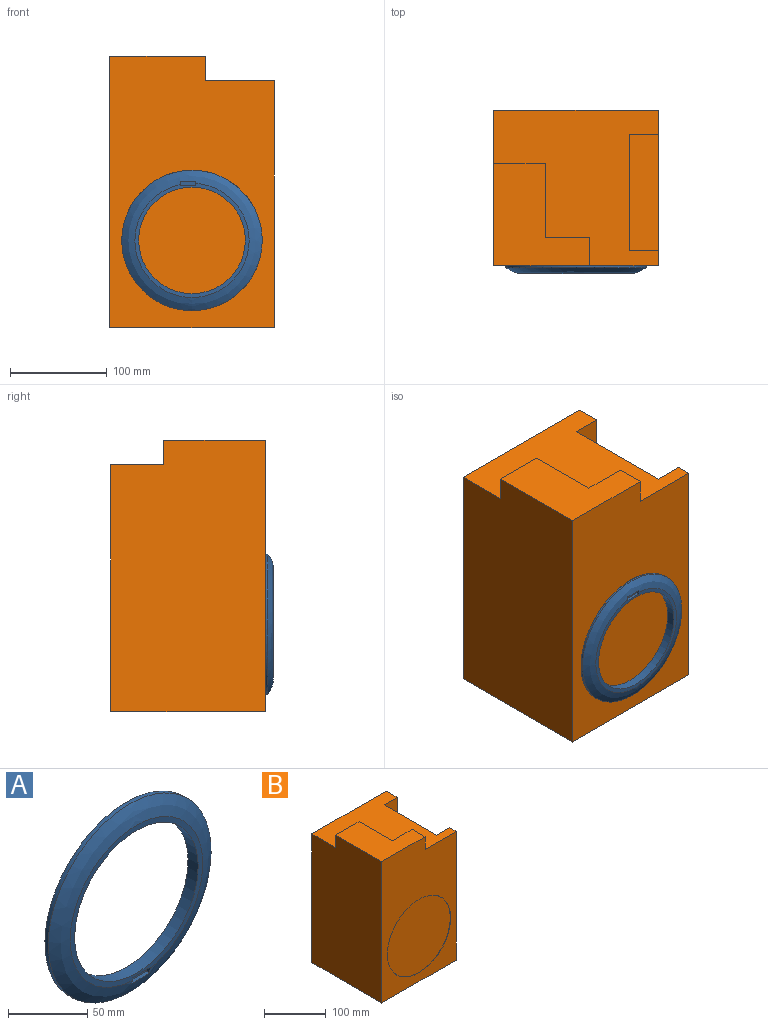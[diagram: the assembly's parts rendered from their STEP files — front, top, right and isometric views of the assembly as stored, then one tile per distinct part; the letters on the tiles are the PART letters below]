
ASSEMBLY  parts=2 mates=1
PART A: 10 faces, bbox 146.1x10.1x146.1 mm
  f0: plane 118.01x117.89mm, normal (0,-1,0), area 1401.7mm2, adj f1,f3,f5,f6,f7
  f1: bspline ~145x145mm, area 6192.6mm2, adj f0,f2,f5,f7,f8
  f2: cylinder r=72.5mm len=145mm, axis (0,1,0), area 1366.6mm2, adj f1,f4
  f3: cylinder r=55mm len=110mm, axis (0,1,0), area 3110.2mm2, adj f0,f4
  f4: plane 145x145mm, normal (0,1,0), area 7009.7mm2, adj f2,f3
  f5: plane 4.21x3.01mm, normal (-1,0,0), area 12.3mm2, adj f0,f1,f6,f8,f9
  f6: plane 15.95x3mm, normal (0,0,-1), area 47.9mm2, adj f0,f5,f7,f9
  f7: plane 4.2x3mm, normal (1,0,0), area 12.5mm2, adj f0,f1,f6,f8,f9
  f8: plane 17.01x3.96mm, normal (0,0,1), area 45.5mm2, adj f1,f5,f7,f9
  f9: plane 15.95x4.2mm, normal (0,-1,0), area 66.9mm2, adj f5,f6,f7,f8
PART B: 17 faces, bbox 170x160x280 mm
  f0: plane 255x160mm, normal (1,0,0), area 31800mm2, adj f1,f3,f4,f5,f8,f9,f10
  f1: plane 170x160mm, normal (0,0,1), area 16661.3mm2, adj f0,f2,f4,f5,f9,f10,f11,f12
  f2: plane 280x160mm, normal (-1,0,0), area 43433.1mm2, adj f1,f3,f4,f5,f12,f16
  f3: plane 170x160mm, normal (0,0,-1), area 27200mm2, adj f0,f2,f4,f5
  f4: plane 280x170mm, normal (0,-1,0), area 29309.9mm2, adj f0,f1,f2,f3,f6,f13,f16
  f5: plane 255x170mm, normal (0,1,0), area 43350mm2, adj f0,f1,f2,f3
  f6: cylinder r=72.5mm len=145mm, axis (0,-1,0), area 455.5mm2, adj f4,f7
  f7: plane 145x145mm, normal (0,-1,0), area 16513mm2, adj f6
  f8: plane 120x30mm, normal (0,0,1), area 3600mm2, adj f0,f9,f10,f11
  f9: plane 75x30mm, normal (0,-1,0), area 2250mm2, adj f0,f1,f8,f11
  f10: plane 75x30mm, normal (0,1,0), area 2250mm2, adj f0,f1,f8,f11
  f11: plane 120x75mm, normal (1,0,0), area 9000mm2, adj f1,f8,f9,f10
  f12: plane 53.16x25mm, normal (0,1,0), area 1329.1mm2, adj f1,f2,f15,f16
  f13: plane 29.27x25mm, normal (1,0,0), area 731.8mm2, adj f1,f4,f14,f16
  f14: plane 45.75x25mm, normal (0,1,0), area 1143.8mm2, adj f1,f13,f15,f16
  f15: plane 76.05x25mm, normal (1,0,0), area 1901.3mm2, adj f1,f12,f14,f16
  f16: plane 105.32x98.92mm, normal (0,0,1), area 6938.7mm2, adj f2,f4,f12,f13,f14,f15
PLACE A rot(axis=(0,1,0),180deg) t=(-133.16,-146.58,-23.55)mm
PLACE B t=(-133.16,12.42,13.95)mm fixed
MATE fastened B.f6 <-> A.f3  axis (0,-1,0) through (-133.16,-146.58,-23.55)mm
